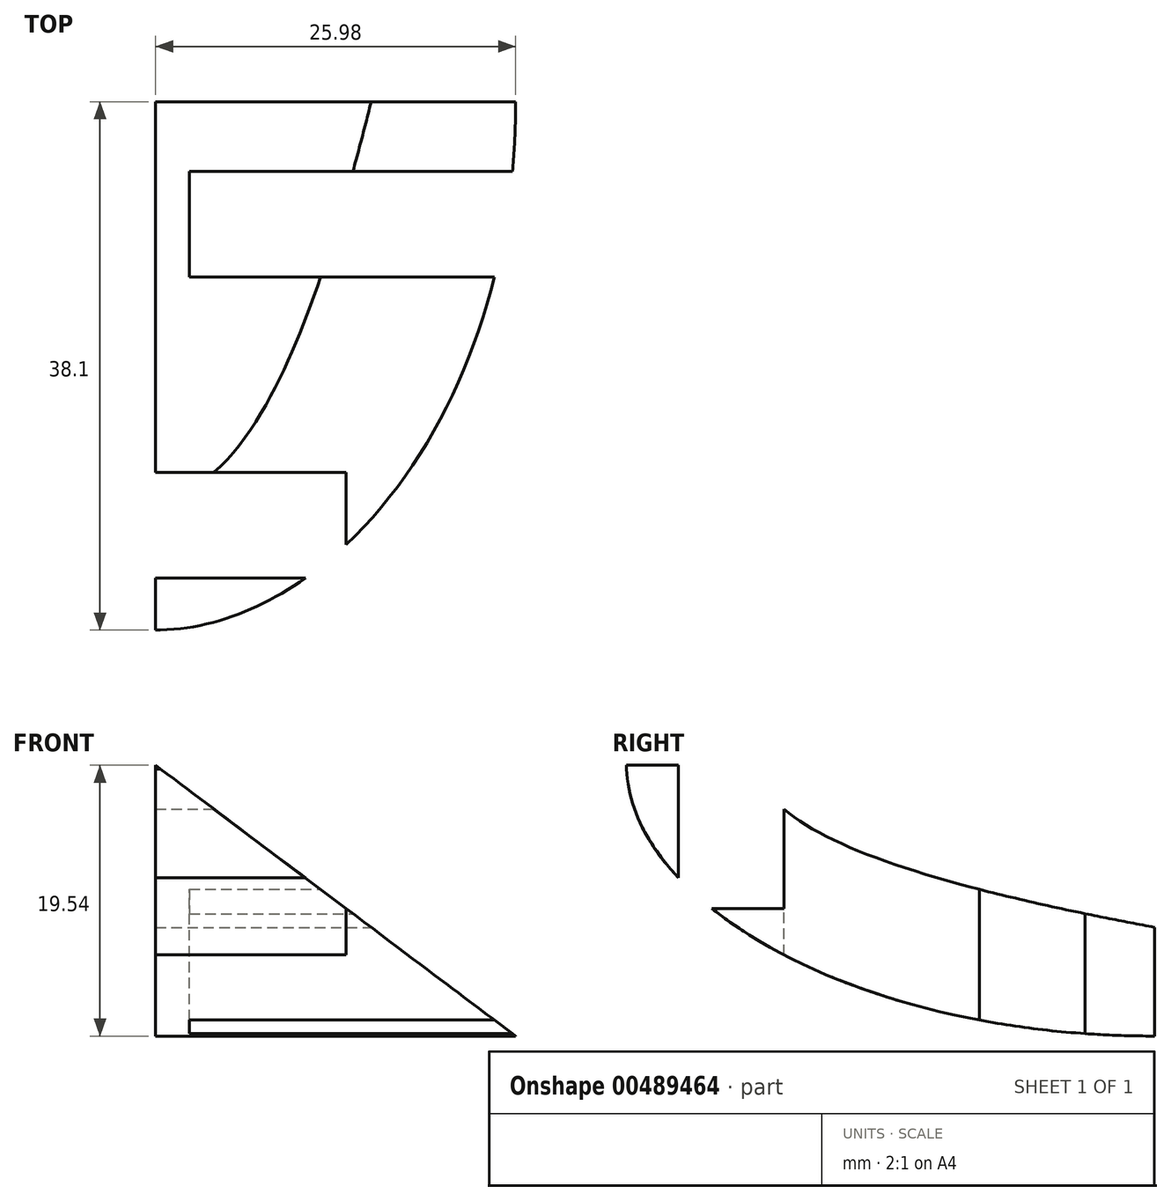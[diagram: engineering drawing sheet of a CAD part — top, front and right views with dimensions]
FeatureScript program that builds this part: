
annotation { "Feature Type Name" : "Feature", "Feature Type Description" : "" }
export const myFeature = defineFeature(function(context is Context, id is Id, definition is map)
    precondition{}
    {
        {
            var Q0;
            Q0=qCreatedBy(makeId("Front.planeOp"),FACE);
            var sketch = newSketch(context, id + "F0", { "sketchPlane" : qUnion([Q0])});
            skLineSegment(sketch, "E0", {"start": v(0, 0) * mm, "end": v(38.1, 0) * mm});
            skLineSegment(sketch, "E1", {"start": v(38.1, 0) * mm, "end": v(38.1, 38.1) * mm});
            skLineSegment(sketch, "E2", {"start": v(38.1, 38.1) * mm, "end": v(0, 38.1) * mm});
            skLineSegment(sketch, "E3", {"start": v(0, 38.1) * mm, "end": v(0, 0) * mm});
            skSolve(sketch);
        }
        {
            var Q0;
            Q0 = qSketchRegion(id + "F0", true);
            extrude(context, id + "F1", {"entities" : qUnion([Q0]), "depth" : 38.1 * mm, "offsetDistance" : 25.4 * mm});
        }
        {
            var Q0;
            Q0=qCreatedBy(makeId("Front.planeOp"),FACE);
            cPlane(context, id + "F2", {"entities" : qUnion([Q0]), "cplaneType" : CPlaneType.OFFSET, "offset" : 38.1 * mm, "width" : 152.4 * mm, "height" : 152.4 * mm});
        }
        {
            var Q0;
            Q0=qCreatedBy(makeId("Right.planeOp"),FACE);
            cPlane(context, id + "F3", {"entities" : qUnion([Q0]), "cplaneType" : CPlaneType.OFFSET, "offset" : 38.1 * mm, "width" : 152.4 * mm, "height" : 152.4 * mm});
        }
        {
            var Q0;
            Q0=qCreatedBy(makeId("Top.planeOp"),FACE);
            cPlane(context, id + "F4", {"entities" : qUnion([Q0]), "cplaneType" : CPlaneType.OFFSET, "offset" : 38.1 * mm, "width" : 152.4 * mm, "height" : 152.4 * mm});
        }
        {
            var Q0;
            Q0=qCreatedBy(id+"F3.planeOp",FACE);
            var sketch = newSketch(context, id + "F5", { "sketchPlane" : qUnion([Q0])});
            skLineSegment(sketch, "E4", {"start": v(-38.1, 38.54) * mm, "end": v(-38.1, 0) * mm});
            skLineSegment(sketch, "E5", {"start": v(-38.1, 0) * mm, "end": v(0, 0) * mm});
            skLineSegment(sketch, "E6", {"start": v(0, 0) * mm, "end": v(0, 38.1) * mm});
            skLineSegment(sketch, "E7", {"start": v(0, 38.1) * mm, "end": v(-38.1, 38.54) * mm});
            skFitSpline(sketch, "E8", {"points": [v(0, 38.1) * mm, v(-38.1, 19.27) * mm, v(0, 0) * mm], "startDerivative": vector(-138.47, 1.61) * mm, "endDerivative": vector(130.17, 0) * mm});
            skLineSegment(sketch, "E9", {"start": v(2.88, 32.71) * mm, "end": v(2.88, 7.31) * mm});
            skFitSpline(sketch, "E10", {"points": [v(2.88, 32.71) * mm, v(-28.37, 19.28) * mm, v(2.88, 7.31) * mm], "startDerivative": vector(-92.43, -2.12) * mm, "endDerivative": vector(89.74, -16.07) * mm});
            skSolve(sketch);
        }
        {
            var Q0;
            {var subQ4=sQuery(id+"F5.wireOp",EDGE,"E9");Q0=makeQuery(id+"F5.imprint","IMPRINT",FACE,{"disambiguationData":[TD([[makeQuery(id+"F5.imprint","IMPRINT",EDGE,{"derivedFrom":subQ4}),-1.0]])]});}
            var Q1;
            {var subQ0=sQuery(id+"F5.wireOp",EDGE,"E10");var subQ1=sQuery(id+"F5.wireOp",EDGE,"E6");var subQ2=makeQuery(id+"F5.imprint","INTERSECT",VERTEX,{"disambiguationData":[OD(0.0)],"derivedFrom":[subQ1,subQ0]});Q1=makeQuery(id+"F5.imprint","IMPRINT",FACE,{"disambiguationData":[TD([[makeQuery(id+"F5.imprint","IMPRINT",EDGE,{"disambiguationData":[TD([[subQ2,-1.0]])],"derivedFrom":subQ1}),1.0]])]});}
            var Q2;
            {var subQ0=sQuery(id+"F5.wireOp",EDGE,"E7");Q2=makeQuery(id+"F5.imprint","IMPRINT",FACE,{"disambiguationData":[TD([[makeQuery(id+"F5.imprint","IMPRINT",EDGE,{"derivedFrom":subQ0}),1.0]])]});}
            var Q3;
            {var subQ0=sQuery(id+"F5.wireOp",EDGE,"E5");Q3=makeQuery(id+"F5.imprint","IMPRINT",FACE,{"disambiguationData":[TD([[makeQuery(id+"F5.imprint","IMPRINT",EDGE,{"derivedFrom":subQ0}),1.0]])]});}
            extrude(context, id + "F6", {"entities" : qUnion([Q0, Q1, Q2, Q3]), "operationType" : NewBodyOperationType.REMOVE, "oppositeDirection" : true, "depth" : 38.1 * mm, "offsetDistance" : 25.4 * mm});
        }
        {
            var Q0;
            Q0=qCreatedBy(id+"F2.planeOp",FACE);
            var sketch = newSketch(context, id + "F7", { "sketchPlane" : qUnion([Q0])});
            skLineSegment(sketch, "E11", {"start": v(0, 0) * mm, "end": v(0, 38.1) * mm});
            skLineSegment(sketch, "E12", {"start": v(0, 38.1) * mm, "end": v(38.1, 38.1) * mm});
            skLineSegment(sketch, "E13", {"start": v(38.1, 38.1) * mm, "end": v(38.1, 0) * mm});
            skLineSegment(sketch, "E14", {"start": v(38.1, 0) * mm, "end": v(0, 0) * mm});
            skLineSegment(sketch, "E15", {"start": v(0, 38.1) * mm, "end": v(0, 0) * mm});
            skLineSegment(sketch, "E16", {"start": v(0, 0) * mm, "end": v(8.2, 0) * mm});
            skLineSegment(sketch, "E17", {"start": v(8.2, 0) * mm, "end": v(8.2, 19.54) * mm});
            skLineSegment(sketch, "E18", {"start": v(8.2, 19.54) * mm, "end": v(34.18, 0) * mm});
            skLineSegment(sketch, "E19", {"start": v(34.18, 0) * mm, "end": v(38.1, 0) * mm});
            skLineSegment(sketch, "E20", {"start": v(38.1, 0) * mm, "end": v(38.1, 4.89) * mm});
            skLineSegment(sketch, "E21", {"start": v(38.1, 4.89) * mm, "end": v(17.25, 19.54) * mm});
            skFitSpline(sketch, "E22", {"points": [v(17.25, 19.54) * mm, v(38.1, 29.92) * mm, v(0, 38.1) * mm], "startDerivative": vector(115.42, -3.36) * mm, "endDerivative": vector(-167.43, 0) * mm});
            skPoint(sketch, "E23", {"position": v(38.1, 19.05) * mm});
            skLineSegment(sketch, "E24", {"start": v(8.2, 35.02) * mm, "end": v(8.2, 22.83) * mm});
            skFitSpline(sketch, "E25", {"points": [v(8.2, 35.02) * mm, v(28.37, 30.14) * mm, v(8.2, 22.83) * mm], "startDerivative": vector(87.83, -6.65) * mm, "endDerivative": vector(-112.95, 6.64) * mm});
            skSolve(sketch);
        }
        {
            var Q0;
            Q0=makeQuery(id+"F7.imprint","IMPRINT",FACE,{"disambiguationData":[TD([[makeQuery(id+"F7.imprint","IMPRINT",EDGE,{"derivedFrom":sQuery(id+"F7.wireOp",EDGE,"E14")}),-1.0]])]});
            var Q1;
            {var subQ0=sQuery(id+"F7.wireOp",EDGE,"E21");Q1=makeQuery(id+"F7.imprint","IMPRINT",FACE,{"disambiguationData":[TD([[makeQuery(id+"F7.imprint","IMPRINT",EDGE,{"derivedFrom":subQ0}),-1.0]])]});}
            var Q2;
            {var subQ0=sQuery(id+"F7.wireOp",EDGE,"E12");Q2=makeQuery(id+"F7.imprint","IMPRINT",FACE,{"disambiguationData":[TD([[makeQuery(id+"F7.imprint","IMPRINT",EDGE,{"derivedFrom":subQ0}),-1.0]])]});}
            var Q3;
            Q3=makeQuery(id+"F7.imprint","IMPRINT",FACE,{"disambiguationData":[TD([[makeQuery(id+"F7.imprint","IMPRINT",EDGE,{"derivedFrom":sQuery(id+"F7.wireOp",EDGE,"E24")}),1.0]])]});
            extrude(context, id + "F8", {"entities" : qUnion([Q0, Q1, Q2, Q3]), "operationType" : NewBodyOperationType.REMOVE, "oppositeDirection" : true, "depth" : 38.1 * mm, "offsetDistance" : 25.4 * mm});
        }
        {
            var Q0;
            Q0=qCreatedBy(id+"F4.planeOp",FACE);
            var sketch = newSketch(context, id + "F9", { "sketchPlane" : qUnion([Q0])});
            skLineSegment(sketch, "E26", {"start": v(0, 0) * mm, "end": v(0, -38.1) * mm});
            skLineSegment(sketch, "E27", {"start": v(0, -38.1) * mm, "end": v(38.1, -38.1) * mm});
            skLineSegment(sketch, "E28", {"start": v(38.1, -38.1) * mm, "end": v(38.1, 0) * mm});
            skLineSegment(sketch, "E29", {"start": v(38.1, 0) * mm, "end": v(0, 0) * mm});
            skLineSegment(sketch, "E30", {"start": v(38.1, -5.01) * mm, "end": v(10.64, -5.01) * mm});
            skLineSegment(sketch, "E31", {"start": v(10.64, -5.01) * mm, "end": v(10.64, -12.63) * mm});
            skLineSegment(sketch, "E32", {"start": v(10.64, -12.63) * mm, "end": v(38.1, -12.63) * mm});
            skLineSegment(sketch, "E33", {"start": v(0, -26.73) * mm, "end": v(21.94, -26.73) * mm});
            skLineSegment(sketch, "E34", {"start": v(21.94, -26.73) * mm, "end": v(21.94, -34.35) * mm});
            skLineSegment(sketch, "E35", {"start": v(21.94, -34.35) * mm, "end": v(0, -34.35) * mm});
            skSolve(sketch);
        }
        {
            var Q0;
            {var subQ0=sQuery(id+"F9.wireOp",EDGE,"E30");Q0=makeQuery(id+"F9.imprint","IMPRINT",FACE,{"disambiguationData":[TD([[makeQuery(id+"F9.imprint","IMPRINT",EDGE,{"derivedFrom":subQ0}),1.0]])]});}
            var Q1;
            {var subQ0=sQuery(id+"F9.wireOp",EDGE,"E33");Q1=makeQuery(id+"F9.imprint","IMPRINT",FACE,{"disambiguationData":[TD([[makeQuery(id+"F9.imprint","IMPRINT",EDGE,{"derivedFrom":subQ0}),-1.0]])]});}
            extrude(context, id + "F10", {"entities" : qUnion([Q0, Q1]), "operationType" : NewBodyOperationType.REMOVE, "oppositeDirection" : true, "depth" : 38.1 * mm, "offsetDistance" : 25.4 * mm});
        }
    });
